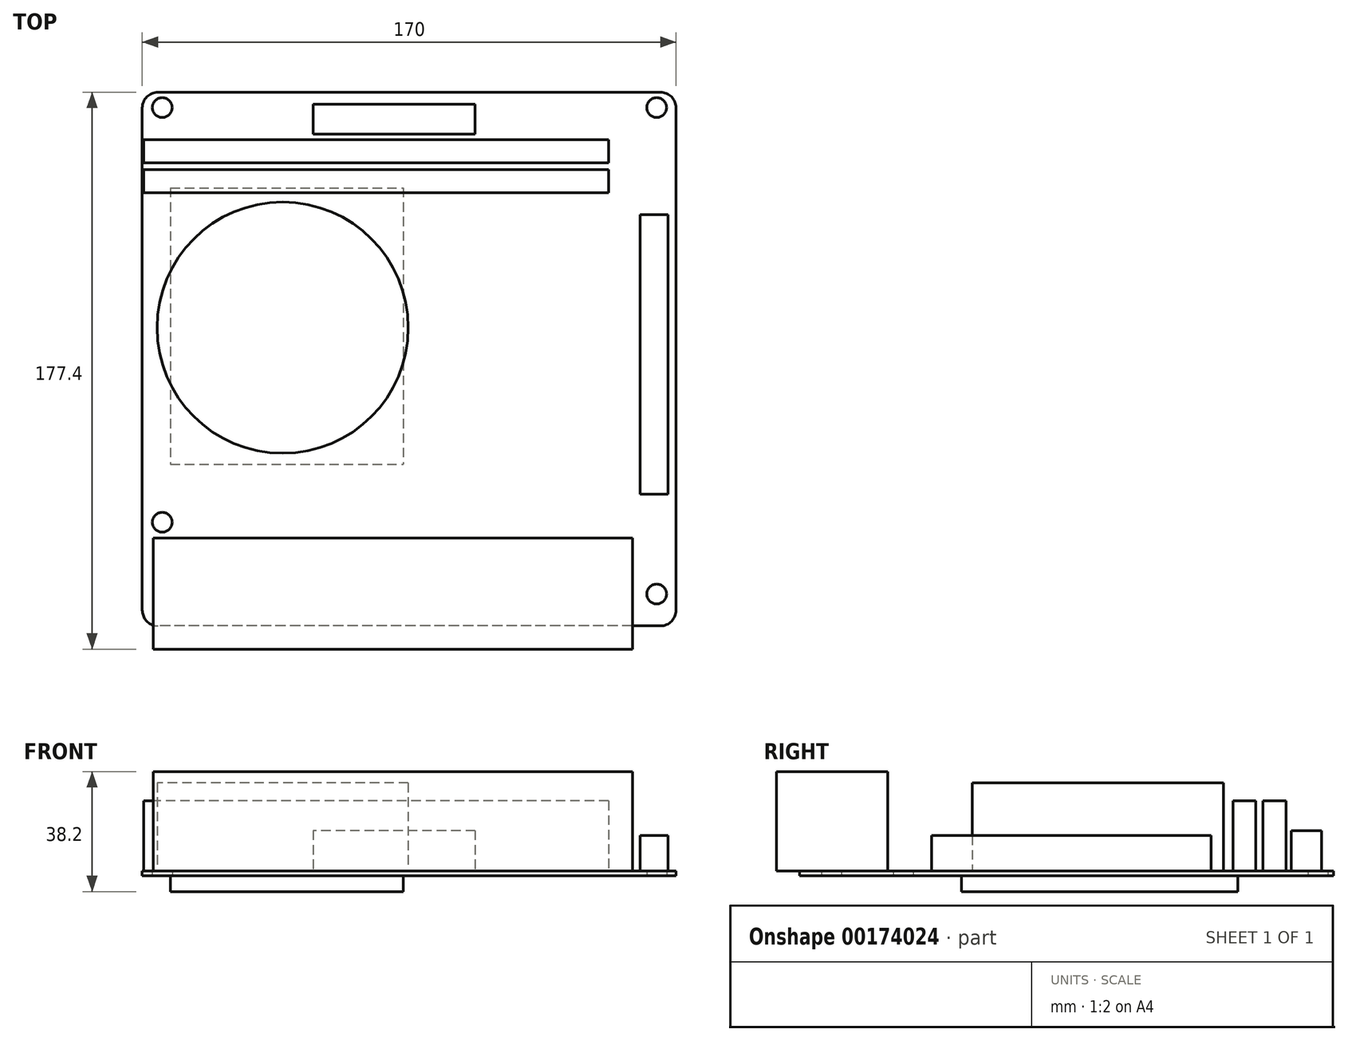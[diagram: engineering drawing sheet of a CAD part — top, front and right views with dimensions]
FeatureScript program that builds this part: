
annotation { "Feature Type Name" : "Feature", "Feature Type Description" : "" }
export const myFeature = defineFeature(function(context is Context, id is Id, definition is map)
    precondition{}
    {
        {
            var Q0;
            Q0=qCreatedBy(makeId("Top.planeOp"),FACE);
            var sketch = newSketch(context, id + "F10", { "sketchPlane" : qUnion([Q0])});
            skLineSegment(sketch, "E0.bottom", {"start": v(85, -85) * mm, "end": v(-85, -85) * mm});
            skLineSegment(sketch, "E0.top", {"start": v(85, 85) * mm, "end": v(-85, 85) * mm});
            skLineSegment(sketch, "E0.left", {"start": v(85, -85) * mm, "end": v(85, 85) * mm});
            skLineSegment(sketch, "E0.right", {"start": v(-85, -85) * mm, "end": v(-85, 85) * mm});
            skPoint(sketch, "E0.middle", {"position": v(0, 0) * mm});
            skCircle(sketch, "E1", {"center": v(-78.65, 80.1) * mm, "radius": 3.18 * mm});
            skCircle(sketch, "E2", {"center": v(78.83, 80.1) * mm, "radius": 3.17 * mm});
            skCircle(sketch, "E3", {"center": v(78.83, -74.84) * mm, "radius": 3.18 * mm});
            skCircle(sketch, "E4", {"center": v(-78.65, -51.98) * mm, "radius": 3.18 * mm});
            skSolve(sketch);
        }
        {
            var Q0;
            Q0=makeQuery(id+"F10.imprint","IMPRINT",FACE,{"disambiguationData":[TD([[makeQuery(id+"F10.imprint","IMPRINT",EDGE,{"derivedFrom":sQuery(id+"F10.wireOp",EDGE,"E0.bottom")}),-1.0]])]});
            extrude(context, id + "F11", {"entities" : qUnion([Q0]), "depth" : 1.6 * mm});
        }
        {
            var Q0;
            Q0=makeQuery(id+"F11.opExtrude","SWEPT_EDGE",EDGE,{"disambiguationData":[OSD([sQuery(id+"F10.wireOp",EDGE,"E0.top"),sQuery(id+"F10.wireOp",EDGE,"E0.right")])]});
            var Q1;
            Q1=makeQuery(id+"F11.opExtrude","SWEPT_EDGE",EDGE,{"disambiguationData":[OSD([sQuery(id+"F10.wireOp",EDGE,"E0.bottom"),sQuery(id+"F10.wireOp",EDGE,"E0.right")])]});
            var Q2;
            Q2=makeQuery(id+"F11.opExtrude","SWEPT_EDGE",EDGE,{"disambiguationData":[OSD([sQuery(id+"F10.wireOp",EDGE,"E0.bottom"),sQuery(id+"F10.wireOp",EDGE,"E0.left")])]});
            var Q3;
            Q3=makeQuery(id+"F11.opExtrude","SWEPT_EDGE",EDGE,{"disambiguationData":[OSD([sQuery(id+"F10.wireOp",EDGE,"E0.top"),sQuery(id+"F10.wireOp",EDGE,"E0.left")])]});
            fillet(context, id + "F0", {"entities" : qUnion([Q0, Q1, Q2, Q3]), "radius" : 5 * mm, "tangentPropagation" : true, "allowEdgeOverflow" : false});
        }
        {
            var Q0;
            Q0=makeQuery(id+"F11.opExtrude","CAP_FACE",FACE,{"disambiguationData":[OSD([sQuery(id+"F10.wireOp",EDGE,"E0.bottom"),sQuery(id+"F10.wireOp",EDGE,"E0.top"),sQuery(id+"F10.wireOp",EDGE,"E0.left"),sQuery(id+"F10.wireOp",EDGE,"E0.right"),sQuery(id+"F10.wireOp",EDGE,"E1"),sQuery(id+"F10.wireOp",EDGE,"E2"),sQuery(id+"F10.wireOp",EDGE,"E3"),sQuery(id+"F10.wireOp",EDGE,"E4")])],"isStart":false});
            var sketch = newSketch(context, id + "F12", { "sketchPlane" : qUnion([Q0])});
            skCircle(sketch, "E5", {"center": v(-40.3, 10) * mm, "radius": 40 * mm});
            skSolve(sketch);
        }
        {
            var Q0;
            Q0=makeQuery(id+"F12.imprint","IMPRINT",FACE,{"disambiguationData":[TD([[makeQuery(id+"F12.imprint","IMPRINT",EDGE,{"derivedFrom":sQuery(id+"F12.wireOp",EDGE,"E5")}),1.0]])]});
            extrude(context, id + "F13", {"entities" : qUnion([Q0]), "depth" : 28 * mm});
        }
        {
            var Q0;
            Q0=makeQuery(id+"F11.opExtrude","CAP_FACE",FACE,{"disambiguationData":[OSD([sQuery(id+"F10.wireOp",EDGE,"E0.bottom"),sQuery(id+"F10.wireOp",EDGE,"E0.top"),sQuery(id+"F10.wireOp",EDGE,"E0.left"),sQuery(id+"F10.wireOp",EDGE,"E0.right"),sQuery(id+"F10.wireOp",EDGE,"E1"),sQuery(id+"F10.wireOp",EDGE,"E2"),sQuery(id+"F10.wireOp",EDGE,"E3"),sQuery(id+"F10.wireOp",EDGE,"E4")])],"isStart":false});
            var sketch = newSketch(context, id + "F1", { "sketchPlane" : qUnion([Q0])});
            skLineSegment(sketch, "E6.bottom", {"start": v(63.5, 60.3) * mm, "end": v(-84.5, 60.3) * mm});
            skLineSegment(sketch, "E6.top", {"start": v(63.5, 52.95) * mm, "end": v(-84.5, 52.95) * mm});
            skLineSegment(sketch, "E6.left", {"start": v(63.5, 60.3) * mm, "end": v(63.5, 52.95) * mm});
            skLineSegment(sketch, "E6.right", {"start": v(-84.5, 60.3) * mm, "end": v(-84.5, 52.95) * mm});
            skLineSegment(sketch, "E7.bottom", {"start": v(63.5, 62.5) * mm, "end": v(-84.5, 62.5) * mm});
            skLineSegment(sketch, "E7.top", {"start": v(63.5, 69.85) * mm, "end": v(-84.5, 69.85) * mm});
            skLineSegment(sketch, "E7.left", {"start": v(63.5, 62.5) * mm, "end": v(63.5, 69.85) * mm});
            skLineSegment(sketch, "E7.right", {"start": v(-84.5, 62.5) * mm, "end": v(-84.5, 69.85) * mm});
            skSolve(sketch);
        }
        {
            var Q0;
            Q0 = qSketchRegion(id + "F1", true);
            extrude(context, id + "F2", {"entities" : qUnion([Q0]), "operationType" : NewBodyOperationType.ADD, "depth" : 22.25 * mm});
        }
        {
            var Q0;
            Q0=makeQuery(id+"F11.opExtrude","CAP_FACE",FACE,{"disambiguationData":[OSD([sQuery(id+"F10.wireOp",EDGE,"E0.bottom"),sQuery(id+"F10.wireOp",EDGE,"E0.top"),sQuery(id+"F10.wireOp",EDGE,"E0.left"),sQuery(id+"F10.wireOp",EDGE,"E0.right"),sQuery(id+"F10.wireOp",EDGE,"E1"),sQuery(id+"F10.wireOp",EDGE,"E2"),sQuery(id+"F10.wireOp",EDGE,"E3"),sQuery(id+"F10.wireOp",EDGE,"E4")])],"isStart":false});
            var sketch = newSketch(context, id + "F14", { "sketchPlane" : qUnion([Q0])});
            skLineSegment(sketch, "E8.bottom", {"start": v(-81.5, -57) * mm, "end": v(71.1, -57) * mm});
            skLineSegment(sketch, "E8.top", {"start": v(-81.5, -92.4) * mm, "end": v(71.1, -92.4) * mm});
            skLineSegment(sketch, "E8.left", {"start": v(-81.5, -57) * mm, "end": v(-81.5, -92.4) * mm});
            skLineSegment(sketch, "E8.right", {"start": v(71.1, -57) * mm, "end": v(71.1, -92.4) * mm});
            skSolve(sketch);
        }
        {
            var Q0;
            Q0 = qSketchRegion(id + "F14", true);
            extrude(context, id + "F3", {"entities" : qUnion([Q0]), "operationType" : NewBodyOperationType.ADD, "depth" : 31.6 * mm});
        }
        {
            var Q0;
            Q0=makeQuery(id+"F11.opExtrude","CAP_FACE",FACE,{"disambiguationData":[OSD([sQuery(id+"F10.wireOp",EDGE,"E0.bottom"),sQuery(id+"F10.wireOp",EDGE,"E0.top"),sQuery(id+"F10.wireOp",EDGE,"E0.left"),sQuery(id+"F10.wireOp",EDGE,"E0.right"),sQuery(id+"F10.wireOp",EDGE,"E1"),sQuery(id+"F10.wireOp",EDGE,"E2"),sQuery(id+"F10.wireOp",EDGE,"E3"),sQuery(id+"F10.wireOp",EDGE,"E4")])],"isStart":true});
            var sketch = newSketch(context, id + "F4", { "sketchPlane" : qUnion([Q0])});
            skLineSegment(sketch, "E9.bottom", {"start": v(-76.02, -54.52) * mm, "end": v(-1.85, -54.52) * mm});
            skLineSegment(sketch, "E9.top", {"start": v(-76.02, 33.48) * mm, "end": v(-1.85, 33.48) * mm});
            skLineSegment(sketch, "E9.left", {"start": v(-76.02, -54.52) * mm, "end": v(-76.02, 33.48) * mm});
            skLineSegment(sketch, "E9.right", {"start": v(-1.85, -54.52) * mm, "end": v(-1.85, 33.48) * mm});
            skSolve(sketch);
        }
        {
            var Q0;
            Q0 = qSketchRegion(id + "F4", true);
            extrude(context, id + "F5", {"entities" : qUnion([Q0]), "depth" : 5 * mm});
        }
        {
            var Q0;
            Q0=makeQuery(id+"F11.opExtrude","CAP_FACE",FACE,{"disambiguationData":[OSD([sQuery(id+"F10.wireOp",EDGE,"E0.bottom"),sQuery(id+"F10.wireOp",EDGE,"E0.top"),sQuery(id+"F10.wireOp",EDGE,"E0.left"),sQuery(id+"F10.wireOp",EDGE,"E0.right"),sQuery(id+"F10.wireOp",EDGE,"E1"),sQuery(id+"F10.wireOp",EDGE,"E2"),sQuery(id+"F10.wireOp",EDGE,"E3"),sQuery(id+"F10.wireOp",EDGE,"E4")])],"isStart":false});
            var sketch = newSketch(context, id + "F6", { "sketchPlane" : qUnion([Q0])});
            skLineSegment(sketch, "E10.bottom", {"start": v(73.6, -43) * mm, "end": v(82.4, -43) * mm});
            skLineSegment(sketch, "E10.top", {"start": v(73.6, 46) * mm, "end": v(82.4, 46) * mm});
            skLineSegment(sketch, "E10.left", {"start": v(73.6, -43) * mm, "end": v(73.6, 46) * mm});
            skLineSegment(sketch, "E10.right", {"start": v(82.4, -43) * mm, "end": v(82.4, 46) * mm});
            skSolve(sketch);
        }
        {
            var Q0;
            Q0 = qSketchRegion(id + "F6", true);
            extrude(context, id + "F7", {"entities" : qUnion([Q0]), "operationType" : NewBodyOperationType.ADD, "depth" : 11.2 * mm});
        }
        {
            var Q0;
            Q0=makeQuery(id+"F11.opExtrude","CAP_FACE",FACE,{"disambiguationData":[OSD([sQuery(id+"F10.wireOp",EDGE,"E0.bottom"),sQuery(id+"F10.wireOp",EDGE,"E0.top"),sQuery(id+"F10.wireOp",EDGE,"E0.left"),sQuery(id+"F10.wireOp",EDGE,"E0.right"),sQuery(id+"F10.wireOp",EDGE,"E1"),sQuery(id+"F10.wireOp",EDGE,"E2"),sQuery(id+"F10.wireOp",EDGE,"E3"),sQuery(id+"F10.wireOp",EDGE,"E4")])],"isStart":false});
            var sketch = newSketch(context, id + "F8", { "sketchPlane" : qUnion([Q0])});
            skLineSegment(sketch, "E11.bottom", {"start": v(21, 71.6) * mm, "end": v(-30.6, 71.6) * mm});
            skLineSegment(sketch, "E11.top", {"start": v(21, 81.2) * mm, "end": v(-30.6, 81.2) * mm});
            skLineSegment(sketch, "E11.left", {"start": v(21, 71.6) * mm, "end": v(21, 81.2) * mm});
            skLineSegment(sketch, "E11.right", {"start": v(-30.6, 71.6) * mm, "end": v(-30.6, 81.2) * mm});
            skSolve(sketch);
        }
        {
            var Q0;
            Q0 = qSketchRegion(id + "F8", true);
            extrude(context, id + "F9", {"entities" : qUnion([Q0]), "operationType" : NewBodyOperationType.ADD, "depth" : 12.8 * mm});
        }
    });
